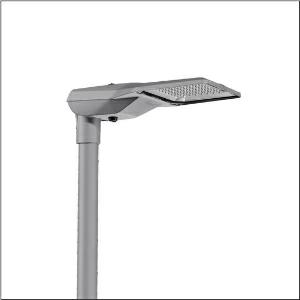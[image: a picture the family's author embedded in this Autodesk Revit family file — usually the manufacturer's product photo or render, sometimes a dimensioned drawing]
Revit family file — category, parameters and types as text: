
# Revit family: streetlight_sl_21_iq_midi___st1_0a_5xe3d31y08nb_4ee3
name_source: partatom
category: Lighting Fixtures
units: mm (PartAtom-declared; Revit-internal decimal feet)

## family parameters
Cut with Voids When Loaded = No
Host = Face
Light Source = No
Part Type = Normal
Room Calculation Point = No
Round Connector Dimension = Use Diameter
Shared = No

## types (1)
- --- (1 x LED, 21550 lm, 136.6 W, 3000K)
    Apparent Load = 137 VA
    CIE Flux Codes = 40 73 97 100 100
    Color Rendering = 70
    Color Temperature = 3000K
    Default Elevation = 1800 mm
    Description = Streetlight SL 21 iQ midi, mast luminaire, primary light control with lens, of PMMA, primary optical cover: cover, of toughened safety glass, transparent, light distribution: ST1.0a, light emission: direct distribution, primary light characteristic: asymmetric, installation type: post-top, side-entry, LED, High Power LED, rated luminous flux: 21.550lm, luminous efficacy: 158lm/W, light colour: 730, colour temperature: 3000K, control gear: iQ-Street Remote, D4i with power reduction, control: pre-setting: logarithmic dimming characteristic, Street-Remote, Auto-Match, Temp-Guard, Lumen-Switch, Night-Set, Smart-Wire, Light-Fading, Desk-Remote (wireless, voltage-free reading and setting of iQ features in the workshop via application-optimized NFC function/RFID function), optimised constant luminous flux control (CLO 2.0), mains connection: 230..240V, AC, 50/60Hz, start of lifetime: 137W, end of service life: 144W, reduction: 61W, luminaire housing, of diecast aluminium, powder-coated, Siteco® metallic grey (DB 702S), corrosivity category C5 high according to DIN EN ISO 12944, please order mast flange separately, inclination adjustable: 0°, 5°, 10°, 15°, sealing non-destructively replaceable, multi-level sealing system, length: 644mm, width: 335mm, height: 110mm, mast flange for spigot size: 42mm (side-entry): 5XC10008XM4, 60/48mm (side-entry/post-top): 5XC10108XM2, 76/60mm (side-entry/post-top): 5XC10108XM1, mounting height: 4..8m, Smart Interface below and above, protection rating (complete): IP66, insulation class (complete): insulation class II (safety insulation), certification: CE, ENEC, ENEC+, VDE, impact resistance: IK10, permissible operating ambient temperature for outdoor applications: -40..+50°C, standard-compliant lighting for roads and squares, packaging unit: 1 piece

Light Distribution: ST1.0a
    Height = 111 mm
    Lamp = 1 x LED
    Lamp Light Flux = 21550 lm
    Lamp Power = 136.6 W
    Lamp count = 1
    Length = 644 mm
    Luminous efficacy = 158 lm/W
    Manufacturer = Siteco
    ModVariant = No
    Model = 5XE3D31Y08NB
    Number of Poles = 1
    OnlyDefault = Yes
    Power Factor = 1
    Product Name = Streetlight SL 21 iQ midi | ST1.0a
    Product group = mast luminaire | pylon top
    ProductGroupID = 6100
    Protection Class = Protection class II
    Protection Degree = IP 66
    RLX_Detail_Level = 1
    RLX_Emergency_Light_Flux = 0 lm
    RLX_Emergency_Type = 0
    RLX_Emergency_Type_DB = No
    RlxData = <blob elided: 91149 chars, md5=aad65412>
    Socket = socket
    Standby Power = 0 W
    System Light Flux = 21550 lm
    System Power = 137 W
    Type Comments = factory setting: luminous flux: 100 % | dim-lin: 254 | 733 mA
    Type Image = l_1004304.jpg
    URL = http://relux.com
    VarID = @adj_117711
    Voltage = 0 V
    Weight = 0.00 kg
    Width = 336 mm

## geometry (parser evidence)
native form markers: Blend x4, Sweep x11
no freeform markers — native parametric forms only
